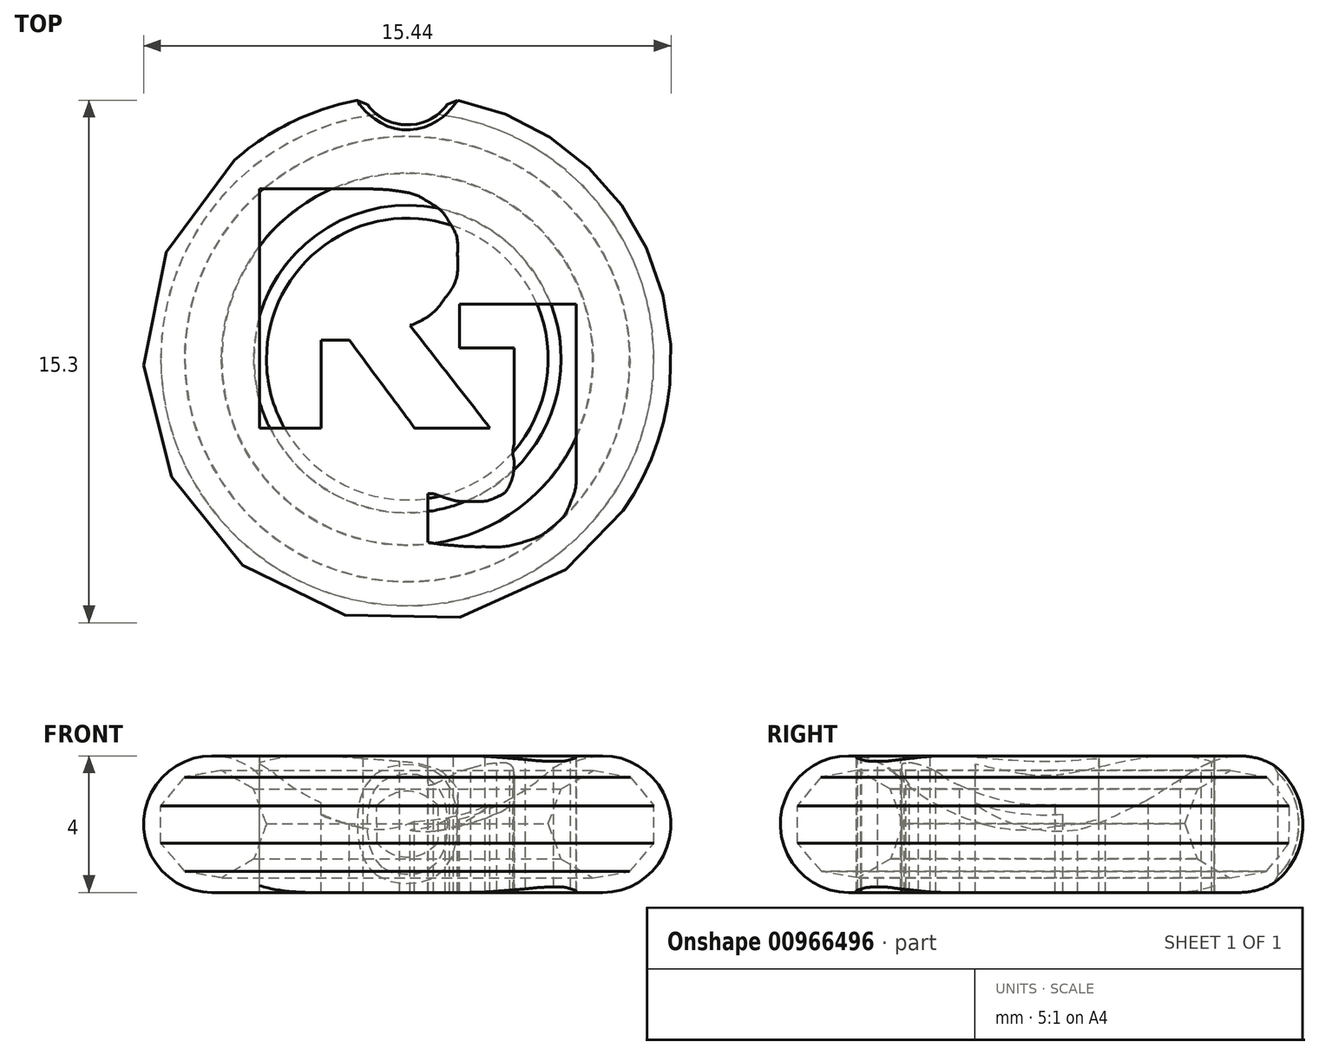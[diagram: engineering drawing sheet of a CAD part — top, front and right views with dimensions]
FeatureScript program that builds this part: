
annotation { "Feature Type Name" : "Feature", "Feature Type Description" : "" }
export const myFeature = defineFeature(function(context is Context, id is Id, definition is map)
    precondition{}
    {
        {
            var Q0;
            Q0=qCreatedBy(makeId("Front.planeOp"),FACE);
            var sketch = newSketch(context, id + "F0", { "sketchPlane" : qUnion([Q0])});
            skArc(sketch, "E0", {"start": v(-4.36, 3.46) * mm, "mid": v(-7.58, 2.73) * mm, "end": v(-5.72, 0) * mm});
            skArc(sketch, "E1", {"start": v(-4.36, 3.46) * mm, "mid": v(-2.34, 2.2) * mm, "end": v(0, 1.75) * mm});
            skLineSegment(sketch, "E2", {"start": v(-5.72, 0) * mm, "end": v(0, 0) * mm});
            skLineSegment(sketch, "E3", {"start": v(0, 0) * mm, "end": v(0, 1.75) * mm});
            skSolve(sketch);
        }
        {
            var Q0;
            Q0=makeQuery(id+"F0.imprint","IMPRINT",FACE,{"disambiguationData":[TD([[makeQuery(id+"F0.imprint","IMPRINT",EDGE,{"derivedFrom":sQuery(id+"F0.wireOp",EDGE,"E0")}),1.0]])]});
            var Q1;
            Q1=sQuery(id+"F0.wireOp",EDGE,"E3");
            revolve(context, id + "F1", {"surfaceOperationType" : NewSurfaceOperationType.NEW, "entities" : qUnion([Q0]), "axis" : qUnion([Q1]), "revolveType" : RevolveType.FULL});
        }
        {
            var Q0;
            Q0=qCreatedBy(makeId("Top.planeOp"),FACE);
            cPlane(context, id + "F2", {"entities" : qUnion([Q0]), "cplaneType" : CPlaneType.OFFSET, "offset" : 8 * mm, "width" : 150 * mm, "height" : 150 * mm});
        }
        {
            var Q0;
            Q0=qCreatedBy(id+"F2.planeOp",FACE);
            var sketch = newSketch(context, id + "F3", { "sketchPlane" : qUnion([Q0])});
            skLineSegment(sketch, "E4", {"start": v(2.42, -2.02) * mm, "end": v(0.21, -2.02) * mm});
            skLineSegment(sketch, "E5", {"start": v(0.21, -2.02) * mm, "end": v(-1.7, 0.55) * mm});
            skLineSegment(sketch, "E6", {"start": v(-1.7, 0.55) * mm, "end": v(-2.53, 0.55) * mm});
            skLineSegment(sketch, "E7", {"start": v(-2.53, 0.55) * mm, "end": v(-2.53, -2.02) * mm});
            skLineSegment(sketch, "E8", {"start": v(-2.53, -2.02) * mm, "end": v(-4.32, -2.02) * mm});
            skLineSegment(sketch, "E9", {"start": v(-4.32, -2.02) * mm, "end": v(-4.32, 4.98) * mm});
            skLineSegment(sketch, "E10", {"start": v(-4.32, 4.98) * mm, "end": v(-1.3, 4.98) * mm});
            skLineSegment(sketch, "E11", {"start": v(0.08, 0.98) * mm, "end": v(2.42, -2.02) * mm});
            skLineSegment(sketch, "E12", {"start": v(0.6, -5.36) * mm, "end": v(0.6, -3.94) * mm});
            skLineSegment(sketch, "E13", {"start": v(0.6, -3.94) * mm, "end": v(0.77, -3.94) * mm});
            skLineSegment(sketch, "E14", {"start": v(3.13, -2.46) * mm, "end": v(3.13, 0.32) * mm});
            skLineSegment(sketch, "E15", {"start": v(3.13, 0.32) * mm, "end": v(1.53, 0.32) * mm});
            skLineSegment(sketch, "E16", {"start": v(1.53, 0.32) * mm, "end": v(1.53, 1.61) * mm});
            skLineSegment(sketch, "E17", {"start": v(1.53, 1.61) * mm, "end": v(4.94, 1.61) * mm});
            skLineSegment(sketch, "E18", {"start": v(4.94, 1.61) * mm, "end": v(4.94, -3.33) * mm});
            skFitSpline(sketch, "E19", {"points": [v(-1.3, 4.98) * mm, v(-0.88, 4.98) * mm, v(-0.53, 4.96) * mm, v(-0.23, 4.91) * mm]});
            skFitSpline(sketch, "E20", {"points": [v(-0.23, 4.91) * mm, v(0.07, 4.86) * mm, v(0.35, 4.76) * mm, v(0.6, 4.6) * mm]});
            skFitSpline(sketch, "E21", {"points": [v(0.6, 4.6) * mm, v(0.87, 4.45) * mm, v(1.08, 4.25) * mm, v(1.23, 4) * mm]});
            skFitSpline(sketch, "E22", {"points": [v(1.23, 4) * mm, v(1.4, 3.75) * mm, v(1.47, 3.44) * mm, v(1.47, 3.06) * mm]});
            skFitSpline(sketch, "E23", {"points": [v(1.47, 3.06) * mm, v(1.47, 2.54) * mm, v(1.35, 2.12) * mm, v(1.1, 1.8) * mm]});
            skFitSpline(sketch, "E24", {"points": [v(1.1, 1.8) * mm, v(0.87, 1.47) * mm, v(0.53, 1.2) * mm, v(0.08, 0.98) * mm]});
            skFitSpline(sketch, "E25", {"points": [v(4.94, -3.33) * mm, v(4.94, -3.64) * mm, v(4.88, -3.93) * mm, v(4.78, -4.2) * mm]});
            skFitSpline(sketch, "E26", {"points": [v(4.78, -4.2) * mm, v(4.67, -4.46) * mm, v(4.5, -4.7) * mm, v(4.29, -4.88) * mm]});
            skFitSpline(sketch, "E27", {"points": [v(4.29, -4.88) * mm, v(4.06, -5.07) * mm, v(3.78, -5.23) * mm, v(3.46, -5.34) * mm]});
            skFitSpline(sketch, "E28", {"points": [v(3.46, -5.34) * mm, v(3.14, -5.44) * mm, v(2.74, -5.5) * mm, v(2.26, -5.5) * mm]});
            skFitSpline(sketch, "E29", {"points": [v(2.26, -5.5) * mm, v(1.94, -5.5) * mm, v(1.63, -5.48) * mm, v(1.35, -5.46) * mm]});
            skFitSpline(sketch, "E30", {"points": [v(1.35, -5.46) * mm, v(1.06, -5.44) * mm, v(0.81, -5.4) * mm, v(0.6, -5.36) * mm]});
            skFitSpline(sketch, "E31", {"points": [v(0.77, -3.94) * mm, v(0.92, -4) * mm, v(1.07, -4.05) * mm, v(1.24, -4.1) * mm]});
            skFitSpline(sketch, "E32", {"points": [v(1.24, -4.1) * mm, v(1.4, -4.15) * mm, v(1.6, -4.17) * mm, v(1.86, -4.17) * mm]});
            skFitSpline(sketch, "E33", {"points": [v(1.86, -4.17) * mm, v(2.19, -4.17) * mm, v(2.44, -4.13) * mm, v(2.62, -4.04) * mm]});
            skFitSpline(sketch, "E34", {"points": [v(2.62, -4.04) * mm, v(2.8, -3.95) * mm, v(2.92, -3.83) * mm, v(3, -3.67) * mm]});
            skFitSpline(sketch, "E35", {"points": [v(3, -3.67) * mm, v(3.07, -3.52) * mm, v(3.11, -3.35) * mm, v(3.12, -3.17) * mm]});
            skFitSpline(sketch, "E36", {"points": [v(3.12, -3.17) * mm, v(3.13, -2.98) * mm, v(3.09, -2.74) * mm, v(3.13, -2.46) * mm]});
            skSolve(sketch);
        }
        {
            var Q0;
            Q0 = qSketchRegion(id + "F3", true);
            extrude(context, id + "F4", {"entities" : qUnion([Q0]), "operationType" : NewBodyOperationType.REMOVE, "oppositeDirection" : true, "depth" : 25 * mm, "offsetDistance" : 25 * mm});
        }
        {
            var Q0;
            Q0=qCreatedBy(makeId("Front.planeOp"),FACE);
            var sketch = newSketch(context, id + "F5", { "sketchPlane" : qUnion([Q0])});
            skCircle(sketch, "E37.cCircle", {"center": v(-5.72, 2) * mm, "radius": 1.5 * mm, "construction": true});
            skLineSegment(sketch, "E37.0", {"start": v(-5.45, 3.57) * mm, "end": v(-4.5, 3.03) * mm});
            skLineSegment(sketch, "E37.1", {"start": v(-4.5, 3.03) * mm, "end": v(-4.12, 2) * mm});
            skLineSegment(sketch, "E37.2", {"start": v(-4.12, 2) * mm, "end": v(-4.5, 0.98) * mm});
            skLineSegment(sketch, "E37.3", {"start": v(-4.5, 0.98) * mm, "end": v(-5.43, 0.43) * mm});
            skLineSegment(sketch, "E37.4", {"start": v(-5.43, 0.43) * mm, "end": v(-6.51, 0.61) * mm});
            skLineSegment(sketch, "E37.5", {"start": v(-6.51, 0.61) * mm, "end": v(-7.22, 1.45) * mm});
            skLineSegment(sketch, "E37.6", {"start": v(-7.22, 1.45) * mm, "end": v(-7.22, 2.54) * mm});
            skLineSegment(sketch, "E37.7", {"start": v(-7.22, 2.54) * mm, "end": v(-6.53, 3.38) * mm});
            skLineSegment(sketch, "E37.8", {"start": v(-6.53, 3.38) * mm, "end": v(-5.45, 3.57) * mm});
            skPoint(sketch, "E37.0.midPoint", {"position": v(-4.98, 3.3) * mm});
            skSolve(sketch);
        }
        {
            var Q0;
            Q0 = qSketchRegion(id + "F5", true);
            var Q1;
            Q1 = qConstructionFilter(qBodyType(qCreatedBy(id + "F5" ,EDGE), BodyType.WIRE), ConstructionObject.NO);
            var Q2;
            Q2=sQuery(id+"F0.wireOp",EDGE,"E3");
            revolve(context, id + "F6", {"surfaceOperationType" : NewSurfaceOperationType.ADD, "entities" : qUnion([Q0]), "surfaceEntities" : qUnion([Q1]), "axis" : qUnion([Q2]), "revolveType" : RevolveType.FULL});
        }
        {
            var Q0;
            Q0=qCreatedBy(id+"F2.planeOp",FACE);
            var sketch = newSketch(context, id + "F7", { "sketchPlane" : qUnion([Q0])});
            skCircle(sketch, "E38", {"center": v(0, 8.3) * mm, "radius": 1.44 * mm});
            skSolve(sketch);
        }
        {
            var Q0;
            Q0 = qSketchRegion(id + "F7", true);
            var Q1;
            Q1=sQuery(id+"F7.wireOp",EDGE,"E38");
            extrude(context, id + "F8", {"entities" : qUnion([Q0]), "operationType" : NewBodyOperationType.REMOVE, "surfaceEntities" : qUnion([Q1]), "oppositeDirection" : true, "depth" : 25 * mm, "offsetDistance" : 25 * mm});
        }
        {
            var Q0;
            Q0=makeQuery(id+"F8.boolean.opBoolean","INTERSECT",EDGE,{"derivedFrom":[makeQuery(id+"F4.boolean.opBoolean","SPLIT",FACE,{"disambiguationData":[TD([makeQuery(id+"F1.opRevolve","SWEPT_FACE",FACE,{"disambiguationData":[OSD([sQuery(id+"F0.wireOp",EDGE,"E2")])]})])],"derivedFrom":makeQuery(id+"F1.opRevolve","SWEPT_FACE",FACE,{"disambiguationData":[OSD([sQuery(id+"F0.wireOp",EDGE,"E0")])]})}),makeQuery(id+"F8.opExtrude","SWEPT_FACE",FACE,{"disambiguationData":[OSD([sQuery(id+"F7.wireOp",EDGE,"E38")])]})]});
            chamfer(context, id + "F9", {"entities" : qUnion([Q0]), "width" : 0.3 * mm, "tangentPropagation" : true});
        }
        {
            var Q0;
            Q0=makeQuery(id+"F7.imprint","IMPRINT",FACE,{"disambiguationData":[TD([[makeQuery(id+"F7.imprint","IMPRINT",EDGE,{"derivedFrom":sQuery(id+"F7.wireOp",EDGE,"E38")}),1.0]])]});
            extrude(context, id + "F10", {"entities" : qUnion([Q0]), "operationType" : NewBodyOperationType.REMOVE, "oppositeDirection" : true, "depth" : 25 * mm, "offsetDistance" : 25 * mm});
        }
    });
